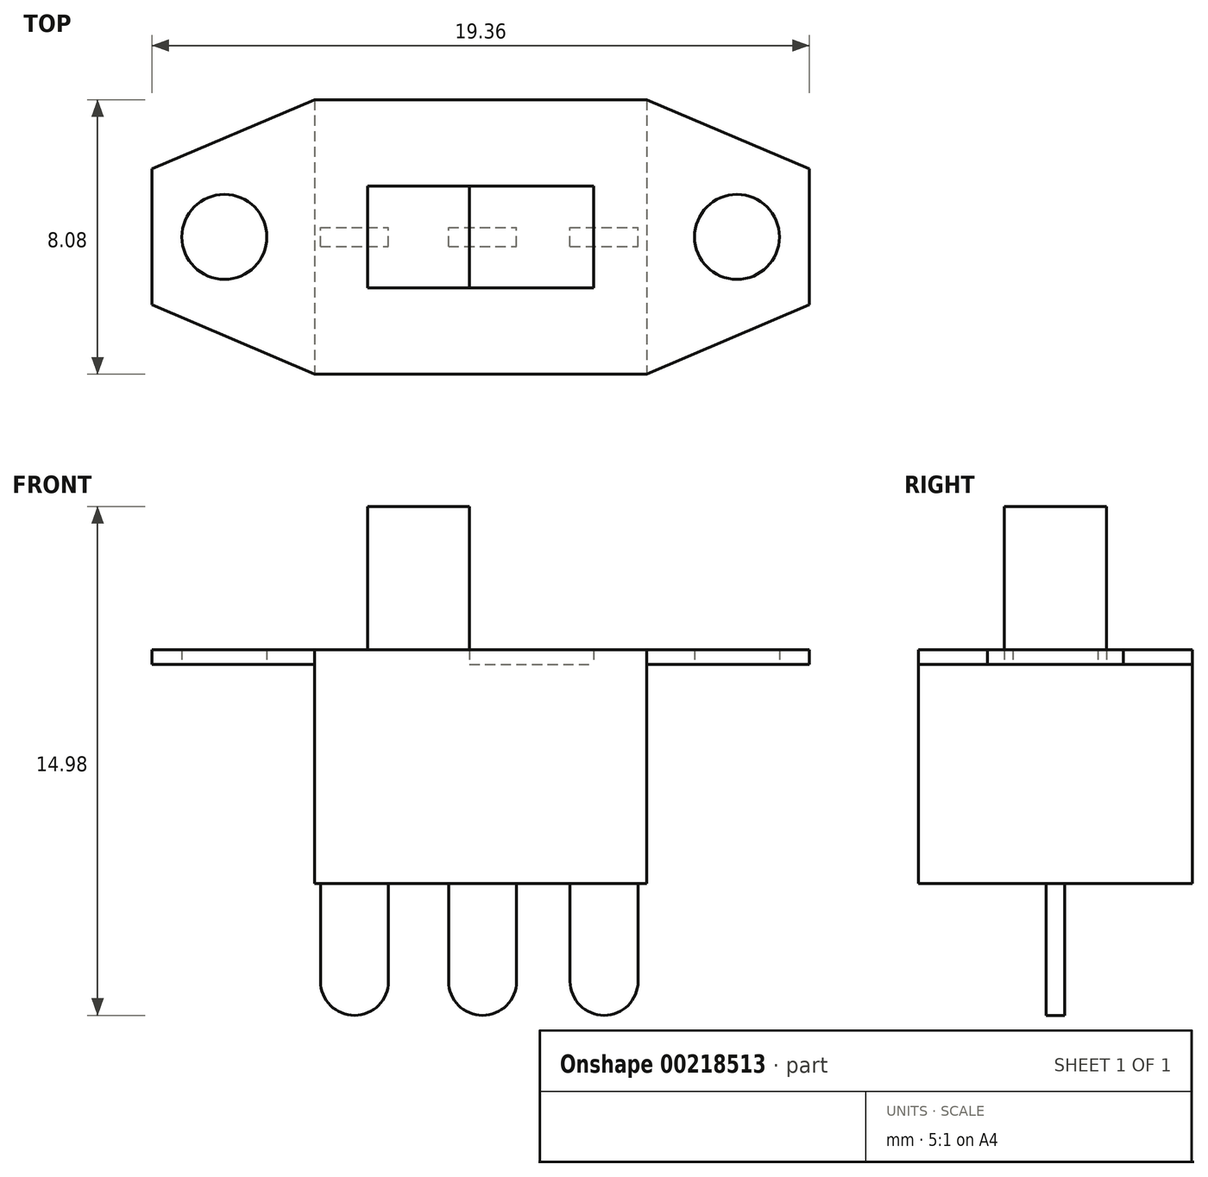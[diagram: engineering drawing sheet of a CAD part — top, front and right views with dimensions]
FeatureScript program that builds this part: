
annotation { "Feature Type Name" : "Feature", "Feature Type Description" : "" }
export const myFeature = defineFeature(function(context is Context, id is Id, definition is map)
    precondition{}
    {
        {
            var Q0;
            Q0=qCreatedBy(makeId("Top.planeOp"),FACE);
            var sketch = newSketch(context, id + "F0", { "sketchPlane" : qUnion([Q0])});
            skLineSegment(sketch, "E0.bottom", {"start": v(-4.89, 4.04) * mm, "end": v(4.89, 4.03) * mm});
            skLineSegment(sketch, "E0.top", {"start": v(-4.89, -4.03) * mm, "end": v(4.89, -4.04) * mm});
            skLineSegment(sketch, "E0.left", {"start": v(-4.88, 4.03) * mm, "end": v(-4.89, -4.03) * mm});
            skLineSegment(sketch, "E0.right", {"start": v(4.89, 4.04) * mm, "end": v(4.88, -4.03) * mm});
            skPoint(sketch, "E1", {"position": v(0, 4.04) * mm});
            skPoint(sketch, "E2", {"position": v(-4.88, 0) * mm});
            skLineSegment(sketch, "E3", {"start": v(-4.88, -4.03) * mm, "end": v(-9.68, -2) * mm});
            skLineSegment(sketch, "E4", {"start": v(-9.68, -2) * mm, "end": v(-9.68, 2) * mm});
            skLineSegment(sketch, "E5", {"start": v(-9.68, 2) * mm, "end": v(-4.88, 4.03) * mm});
            skPoint(sketch, "E6", {"position": v(-9.68, 0) * mm});
            skLineSegment(sketch, "E7", {"start": v(0, 4.04) * mm, "end": v(0, 0) * mm, "construction": true});
            skLineSegment(sketch, "E8", {"start": v(0, 0) * mm, "end": v(-4.88, 0) * mm, "construction": true});
            skLineSegment(sketch, "E9.MirrorCS", {"start": v(4.88, -4.04) * mm, "end": v(9.68, -2) * mm});
            skLineSegment(sketch, "E10.MirrorCS", {"start": v(9.68, 2) * mm, "end": v(4.88, 4.03) * mm});
            skLineSegment(sketch, "E11.MirrorCS", {"start": v(9.68, -2) * mm, "end": v(9.68, 2) * mm});
            skCircle(sketch, "E12", {"center": v(-7.55, 0) * mm, "radius": 1.25 * mm});
            skCircle(sketch, "E13.MirrorC", {"center": v(7.55, 0) * mm, "radius": 1.25 * mm});
            skLineSegment(sketch, "E14.bottom", {"start": v(-3.33, 1.5) * mm, "end": v(3.33, 1.5) * mm});
            skLineSegment(sketch, "E14.top", {"start": v(-3.33, -1.5) * mm, "end": v(3.33, -1.5) * mm});
            skLineSegment(sketch, "E14.left", {"start": v(-3.33, 1.5) * mm, "end": v(-3.33, -1.5) * mm});
            skLineSegment(sketch, "E14.right", {"start": v(3.33, 1.5) * mm, "end": v(3.33, -1.5) * mm});
            skPoint(sketch, "E15", {"position": v(0, -1.5) * mm});
            skPoint(sketch, "E16", {"position": v(3.33, 0) * mm});
            skLineSegment(sketch, "E17", {"start": v(-0.33, 1.5) * mm, "end": v(-0.33, -1.5) * mm});
            skSolve(sketch);
        }
        {
            var Q0;
            {var subQ0=sQuery(id+"F0.wireOp",EDGE,"E14.left");Q0=makeQuery(id+"F0.imprint","IMPRINT",FACE,{"disambiguationData":[TD([[makeQuery(id+"F0.imprint","IMPRINT",EDGE,{"derivedFrom":subQ0}),1.0]])]});}
            extrude(context, id + "F1", {"entities" : qUnion([Q0]), "depth" : 4.65 * mm});
        }
        {
            var Q0;
            Q0=makeQuery(id+"F0.imprint","IMPRINT",FACE,{"disambiguationData":[TD([[makeQuery(id+"F0.imprint","IMPRINT",EDGE,{"derivedFrom":sQuery(id+"F0.wireOp",EDGE,"E0.bottom")}),-1.0]])]});
            var Q1;
            {var subQ0=sQuery(id+"F0.wireOp",EDGE,"E14.right");Q1=makeQuery(id+"F0.imprint","IMPRINT",FACE,{"disambiguationData":[TD([[makeQuery(id+"F0.imprint","IMPRINT",EDGE,{"derivedFrom":subQ0}),-1.0]])]});}
            var Q2;
            {var subQ0=sQuery(id+"F0.wireOp",EDGE,"E14.left");Q2=makeQuery(id+"F0.imprint","IMPRINT",FACE,{"disambiguationData":[TD([[makeQuery(id+"F0.imprint","IMPRINT",EDGE,{"derivedFrom":subQ0}),1.0]])]});}
            extrude(context, id + "F2", {"entities" : qUnion([Q0, Q1, Q2]), "operationType" : NewBodyOperationType.ADD, "oppositeDirection" : true, "depth" : 6.45 * mm});
        }
        {
            var Q0;
            Q0=makeQuery(id+"F0.imprint","IMPRINT",FACE,{"disambiguationData":[TD([[makeQuery(id+"F0.imprint","IMPRINT",EDGE,{"derivedFrom":sQuery(id+"F0.wireOp",EDGE,"E0.left")}),-1.0]])]});
            var Q1;
            Q1=makeQuery(id+"F0.imprint","IMPRINT",FACE,{"disambiguationData":[TD([[makeQuery(id+"F0.imprint","IMPRINT",EDGE,{"derivedFrom":sQuery(id+"F0.wireOp",EDGE,"E0.bottom")}),-1.0]])]});
            var Q2;
            Q2=makeQuery(id+"F0.imprint","IMPRINT",FACE,{"disambiguationData":[TD([[makeQuery(id+"F0.imprint","IMPRINT",EDGE,{"derivedFrom":sQuery(id+"F0.wireOp",EDGE,"E0.right")}),1.0]])]});
            extrude(context, id + "F3", {"entities" : qUnion([Q0, Q1, Q2]), "operationType" : NewBodyOperationType.ADD, "depth" : .44 * mm});
        }
        {
            var Q0;
            Q0=makeQuery(id+"F2.opExtrude","CAP_FACE",FACE,{"disambiguationData":[OSD([sQuery(id+"F0.wireOp",EDGE,"E0.bottom"),sQuery(id+"F0.wireOp",EDGE,"E0.top"),sQuery(id+"F0.wireOp",EDGE,"E0.left"),sQuery(id+"F0.wireOp",EDGE,"E0.right")])],"isStart":false});
            var sketch = newSketch(context, id + "F4", { "sketchPlane" : qUnion([Q0])});
            skLineSegment(sketch, "E18.bottom", {"start": v(-4.72, 0.27) * mm, "end": v(4.63, 0.27) * mm});
            skLineSegment(sketch, "E18.top", {"start": v(-4.72, -0.27) * mm, "end": v(4.63, -0.27) * mm});
            skLineSegment(sketch, "E18.left", {"start": v(-4.72, 0.27) * mm, "end": v(-4.72, -0.27) * mm});
            skLineSegment(sketch, "E18.right", {"start": v(4.63, 0.27) * mm, "end": v(4.63, -0.27) * mm});
            skLineSegment(sketch, "E19.0", {"start": v(-4.88, -4.04) * mm, "end": v(-4.89, 4.03) * mm});
            skLineSegment(sketch, "E20.0", {"start": v(4.89, -4.04) * mm, "end": v(4.88, 4.03) * mm});
            skPoint(sketch, "E21", {"position": v(-4.88, 0) * mm});
            skPoint(sketch, "E22", {"position": v(-4.72, 0) * mm});
            skLineSegment(sketch, "E23", {"start": v(-2.72, 0.27) * mm, "end": v(-2.72, -0.27) * mm});
            skLineSegment(sketch, "E24", {"start": v(-0.95, 0.27) * mm, "end": v(-0.95, -0.27) * mm});
            skLineSegment(sketch, "E25", {"start": v(1.05, 0.27) * mm, "end": v(1.05, -0.27) * mm});
            skLineSegment(sketch, "E26", {"start": v(2.63, 0.27) * mm, "end": v(2.63, -0.27) * mm});
            skSolve(sketch);
        }
        {
            var Q0;
            {var subQ0=sQuery(id+"F4.wireOp",EDGE,"E18.left");Q0=makeQuery(id+"F4.imprint","IMPRINT",FACE,{"disambiguationData":[TD([[makeQuery(id+"F4.imprint","IMPRINT",EDGE,{"derivedFrom":subQ0}),1.0]])]});}
            var Q1;
            {var subQ0=sQuery(id+"F4.wireOp",EDGE,"E24");Q1=makeQuery(id+"F4.imprint","IMPRINT",FACE,{"disambiguationData":[TD([[makeQuery(id+"F4.imprint","IMPRINT",EDGE,{"derivedFrom":subQ0}),1.0]])]});}
            var Q2;
            {var subQ0=sQuery(id+"F4.wireOp",EDGE,"E18.right");Q2=makeQuery(id+"F4.imprint","IMPRINT",FACE,{"disambiguationData":[TD([[makeQuery(id+"F4.imprint","IMPRINT",EDGE,{"derivedFrom":subQ0}),-1.0]])]});}
            extrude(context, id + "F5", {"entities" : qUnion([Q0, Q1, Q2]), "operationType" : NewBodyOperationType.ADD, "depth" : 3.88 * mm});
        }
        {
            var Q0;
            Q0=makeQuery(id+"F5.opExtrude","CAP_EDGE",EDGE,{"disambiguationData":[OSD([sQuery(id+"F4.wireOp",EDGE,"E23")])],"isStart":false});
            var Q1;
            Q1=makeQuery(id+"F5.opExtrude","CAP_EDGE",EDGE,{"disambiguationData":[OSD([sQuery(id+"F4.wireOp",EDGE,"E18.left")])],"isStart":false});
            var Q2;
            Q2=makeQuery(id+"F5.opExtrude","CAP_EDGE",EDGE,{"disambiguationData":[OSD([sQuery(id+"F4.wireOp",EDGE,"E24")])],"isStart":false});
            var Q3;
            Q3=makeQuery(id+"F5.opExtrude","CAP_EDGE",EDGE,{"disambiguationData":[OSD([sQuery(id+"F4.wireOp",EDGE,"E25")])],"isStart":false});
            var Q4;
            Q4=makeQuery(id+"F5.opExtrude","CAP_EDGE",EDGE,{"disambiguationData":[OSD([sQuery(id+"F4.wireOp",EDGE,"E26")])],"isStart":false});
            var Q5;
            Q5=makeQuery(id+"F5.opExtrude","CAP_EDGE",EDGE,{"disambiguationData":[OSD([sQuery(id+"F4.wireOp",EDGE,"E18.right")])],"isStart":false});
            fillet(context, id + "F6", {"entities" : qUnion([Q0, Q1, Q2, Q3, Q4, Q5]), "radius" : 1 * mm, "tangentPropagation" : true, "allowEdgeOverflow" : false});
        }
    });
